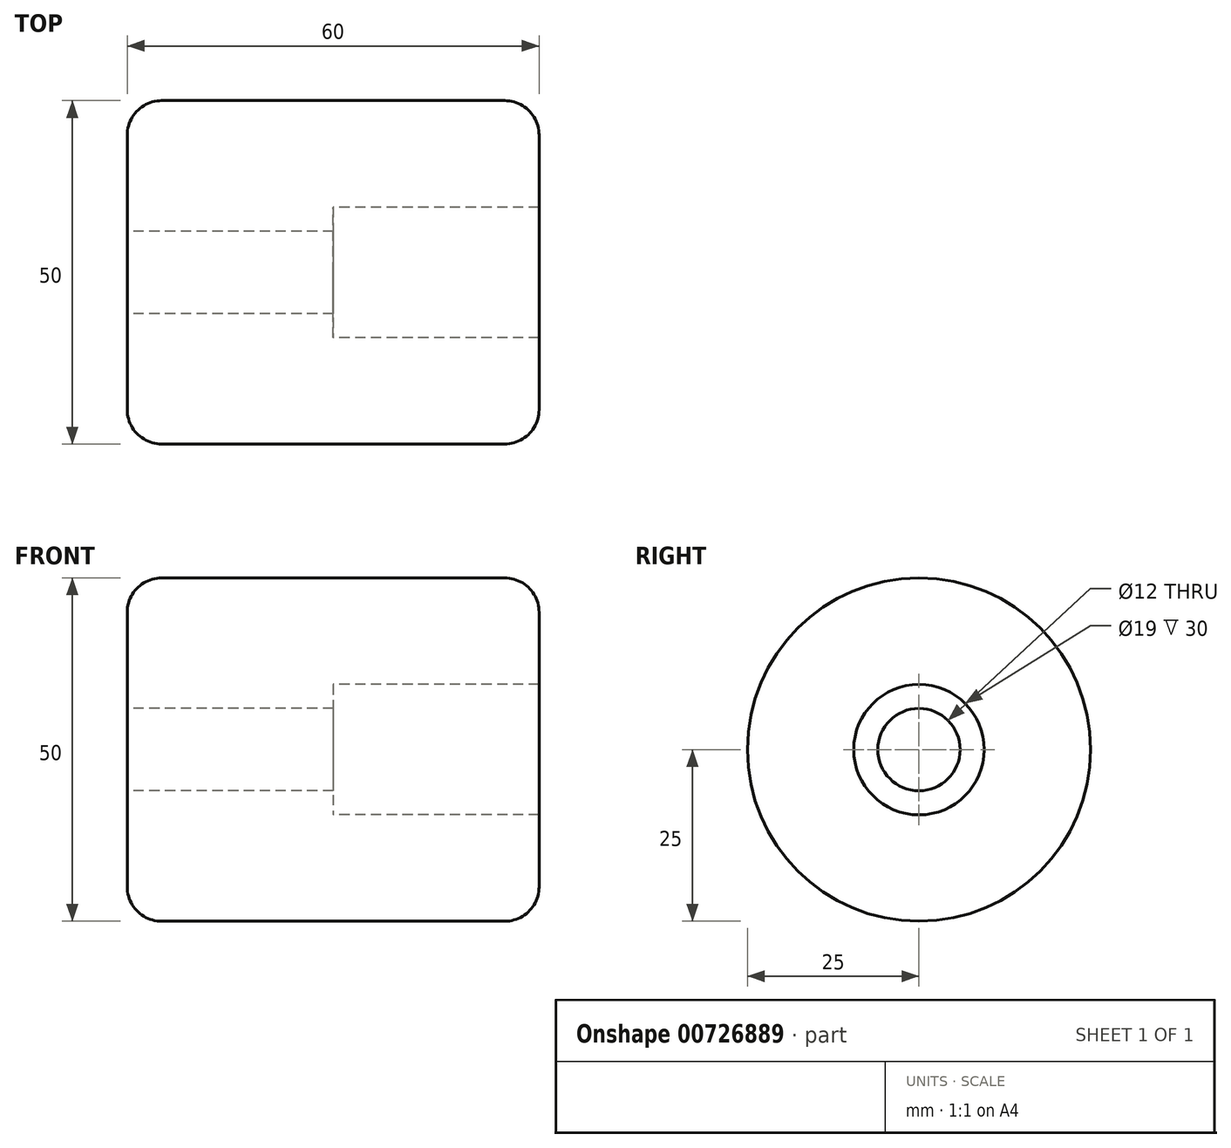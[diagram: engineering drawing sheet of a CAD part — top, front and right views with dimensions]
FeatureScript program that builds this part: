
annotation { "Feature Type Name" : "Feature", "Feature Type Description" : "" }
export const myFeature = defineFeature(function(context is Context, id is Id, definition is map)
    precondition{}
    {
        {
            var Q0;
            Q0=qCreatedBy(makeId("Front.planeOp"),FACE);
            var sketch = newSketch(context, id + "F0", { "sketchPlane" : qUnion([Q0])});
            skLineSegment(sketch, "E0", {"start": v(0, 6) * mm, "end": v(0, 25) * mm});
            skLineSegment(sketch, "E1", {"start": v(0, 25) * mm, "end": v(60, 25) * mm});
            skLineSegment(sketch, "E2", {"start": v(60, 25) * mm, "end": v(60, 9.5) * mm});
            skLineSegment(sketch, "E3", {"start": v(0, 6) * mm, "end": v(30, 6) * mm});
            skPoint(sketch, "E4.endSnap0", {"position": v(30, 6) * mm});
            skLineSegment(sketch, "E5", {"start": v(30, 9.5) * mm, "end": v(30, 6) * mm});
            skLineSegment(sketch, "E6", {"start": v(60, 9.5) * mm, "end": v(30, 9.5) * mm});
            skPoint(sketch, "E7.start.orphan", {"position": v(60, 6) * mm});
            skPoint(sketch, "E8.trimOffspring.end.orphan", {"position": v(60, 0) * mm});
            skLineSegment(sketch, "E9", {"start": v(0, 0) * mm, "end": v(60, 0) * mm, "construction": true});
            skSolve(sketch);
        }
        {
            var Q0;
            Q0=makeQuery(id+"F0.imprint","IMPRINT",FACE,{"disambiguationData":[TD([[makeQuery(id+"F0.imprint","IMPRINT",EDGE,{"derivedFrom":sQuery(id+"F0.wireOp",EDGE,"E0")}),-1.0]])]});
            var Q1;
            Q1=sQuery(id+"F0.wireOp",EDGE,"E9");
            revolve(context, id + "F1", {"surfaceOperationType" : NewSurfaceOperationType.NEW, "entities" : qUnion([Q0]), "axis" : qUnion([Q1]), "revolveType" : RevolveType.FULL});
        }
        {
            var Q0;
            Q0=makeQuery(id+"F1.opRevolve","SWEPT_EDGE",EDGE,{"disambiguationData":[OSD([sQuery(id+"F0.wireOp",EDGE,"E0"),sQuery(id+"F0.wireOp",EDGE,"E1")])]});
            var Q1;
            Q1=makeQuery(id+"F1.opRevolve","SWEPT_EDGE",EDGE,{"disambiguationData":[OSD([sQuery(id+"F0.wireOp",EDGE,"E1"),sQuery(id+"F0.wireOp",EDGE,"E2")])]});
            fillet(context, id + "F2", {"entities" : qUnion([Q0, Q1]), "radius" : 5 * mm, "tangentPropagation" : true, "allowEdgeOverflow" : false});
        }
    });
